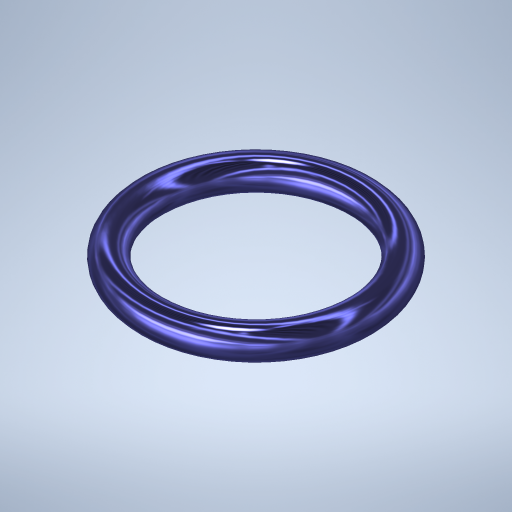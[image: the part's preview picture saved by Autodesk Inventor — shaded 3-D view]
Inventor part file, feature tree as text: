
AUTODESK INVENTOR PART (.ipt)
format: ipt  version: 2023.1 (Build 271208000, 208)  size: 334,848 bytes
history: native  units: in
note: dims shown in document units (in); Inventor stores cm internally (conversion verified against a paired STEP export)
features: revolve x1, sketch x1
ambient origin geometry x8: Origin, YZ Plane, XZ Plane, XY Plane, X Axis, Y Axis, Z Axis, Center Point
bodies: Solid1 (feature_tree)
feature tree (2):
  revolve  "Revolution1"  [1 undecoded]
  sketch  "Sketch2"  dims[d0=0.0625in d1=0.2117in d2=90.0deg]
note: 1 required parameter value undecoded (feature->parameter linkage not recoverable at this tier; creation-order binding heuristic only, values carry confidence <= 0.55)
